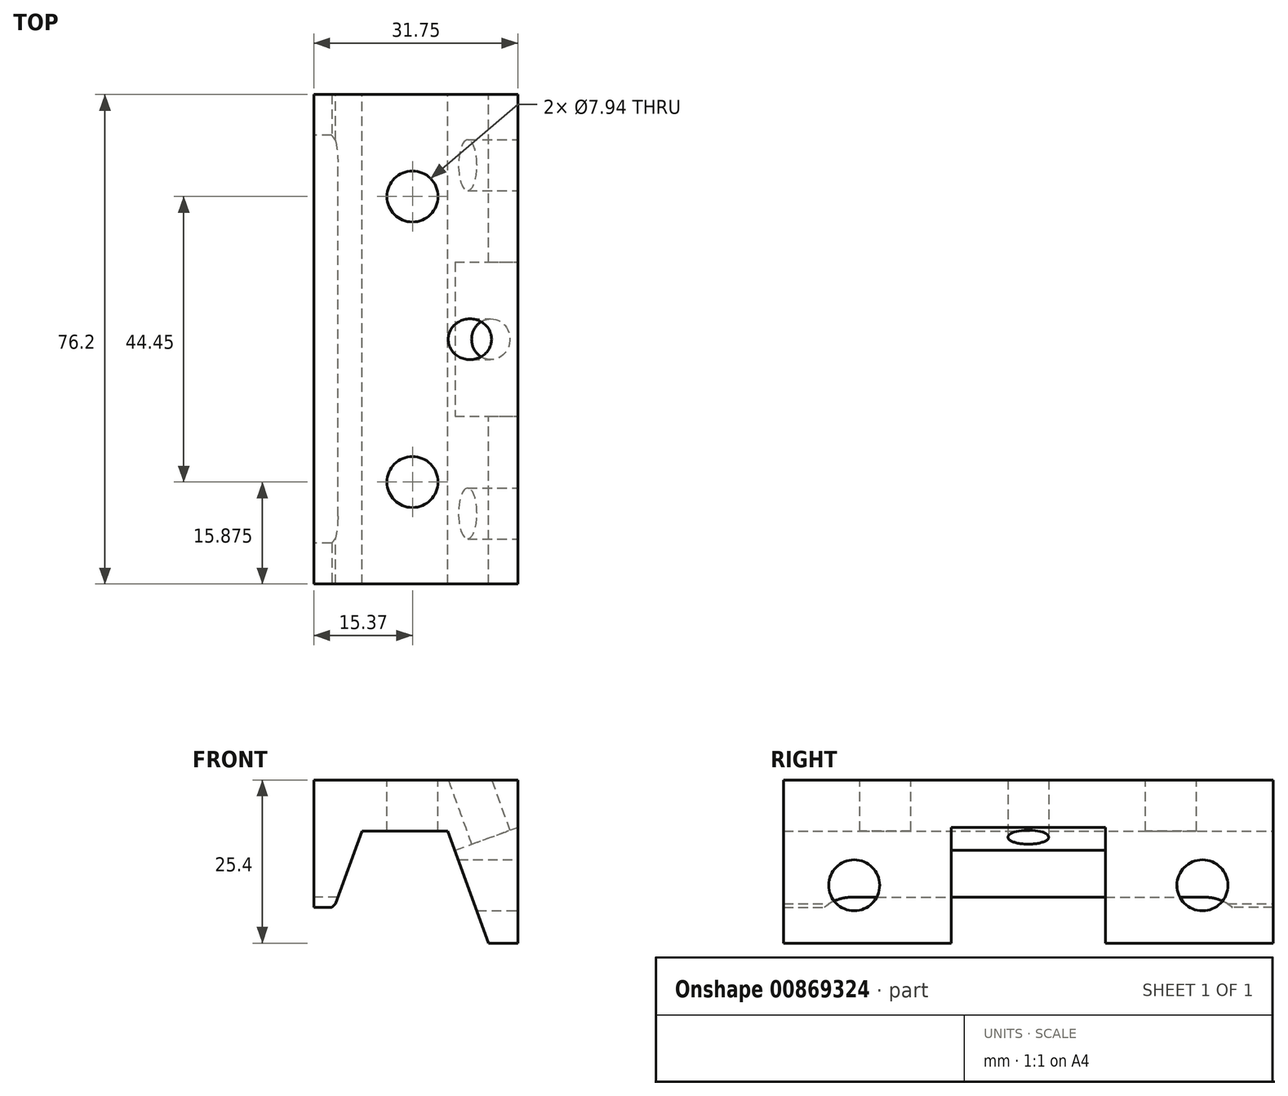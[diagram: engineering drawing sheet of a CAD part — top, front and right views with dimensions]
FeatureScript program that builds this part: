
annotation { "Feature Type Name" : "Feature", "Feature Type Description" : "" }
export const myFeature = defineFeature(function(context is Context, id is Id, definition is map)
    precondition{}
    {
        {
            var Q0;
            Q0=qCreatedBy(makeId("Front.planeOp"),FACE);
            var sketch = newSketch(context, id + "F0", { "sketchPlane" : qUnion([Q0])});
            skLineSegment(sketch, "E0", {"start": v(-7.86, 17.46) * mm, "end": v(5.5, 17.46) * mm});
            skLineSegment(sketch, "E1", {"start": v(-12.2, 5.56) * mm, "end": v(-15.37, 5.56) * mm});
            skLineSegment(sketch, "E2", {"start": v(11.86, 0) * mm, "end": v(16.38, 0) * mm});
            skLineSegment(sketch, "E3", {"start": v(-7.86, 17.46) * mm, "end": v(-12.2, 5.56) * mm});
            skLineSegment(sketch, "E4", {"start": v(5.5, 17.46) * mm, "end": v(11.86, 0) * mm});
            skPoint(sketch, "E5", {"position": v(8.69, 8.73) * mm});
            skPoint(sketch, "E5.positionSnap0", {"position": v(8.69, 8.73) * mm});
            skPoint(sketch, "E6", {"position": v(0, 17.46) * mm});
            skLineSegment(sketch, "E7", {"start": v(-15.37, 5.56) * mm, "end": v(-15.37, 25.4) * mm});
            skLineSegment(sketch, "E8", {"start": v(-15.37, 25.4) * mm, "end": v(16.38, 25.4) * mm});
            skLineSegment(sketch, "E9", {"start": v(6.6, 14.46) * mm, "end": v(16.38, 18.02) * mm});
            skLineSegment(sketch, "E10", {"start": v(29.07, 14.12) * mm, "end": v(9.34, 6.94) * mm});
            skLineSegment(sketch, "E11", {"start": v(16.38, 25.4) * mm, "end": v(16.38, 0) * mm});
            skPoint(sketch, "E12", {"position": v(19.2, 10.53) * mm});
            skSolve(sketch);
        }
        {
            var Q0;
            {var subQ0=sQuery(id+"F0.wireOp",EDGE,"wyo1lMDk-e6bC-kYg6-a8j1-Ru8ALgOuLrMR");var subQ1=sQuery(id+"F0.wireOp",EDGE,"E9");var subQ2=makeQuery(id+"F0.imprint","INTERSECT",VERTEX,{"derivedFrom":[subQ1,subQ0]});Q0=makeQuery(id+"F0.imprint","IMPRINT",FACE,{"disambiguationData":[TD([[makeQuery(id+"F0.imprint","IMPRINT",EDGE,{"disambiguationData":[TD([[subQ2,1.0]])],"derivedFrom":subQ1}),-1.0]])]});}
            var Q1;
            {var subQ5=sQuery(id+"F0.wireOp",EDGE,"E0");Q1=makeQuery(id+"F0.imprint","IMPRINT",FACE,{"disambiguationData":[TD([[makeQuery(id+"F0.imprint","IMPRINT",EDGE,{"derivedFrom":subQ5}),1.0]])]});}
            var Q2;
            {var subQ0=sQuery(id+"F0.wireOp",EDGE,"E9");var subQ1=sQuery(id+"F0.wireOp",EDGE,"E4");var subQ2=makeQuery(id+"F0.imprint","INTERSECT",VERTEX,{"derivedFrom":[subQ1,subQ0]});Q2=makeQuery(id+"F0.imprint","IMPRINT",FACE,{"disambiguationData":[TD([[makeQuery(id+"F0.imprint","IMPRINT",EDGE,{"disambiguationData":[TD([[subQ2,-1.0]])],"derivedFrom":subQ1}),1.0]])]});}
            var Q3;
            {var subQ5=sQuery(id+"F0.wireOp",EDGE,"MGBtKP5I-cxsz-jBet-ha0O-NG6443iWrkXD.bottom");Q3=makeQuery(id+"F0.imprint","IMPRINT",FACE,{"disambiguationData":[TD([[makeQuery(id+"F0.imprint","IMPRINT",EDGE,{"derivedFrom":subQ5}),1.0]])]});}
            var Q4;
            {var subQ3=sQuery(id+"F0.wireOp",EDGE,"MGBtKP5I-cxsz-jBet-ha0O-NG6443iWrkXD.left");var subQ5=sQuery(id+"F0.wireOp",EDGE,"E9");var subQ6=makeQuery(id+"F0.imprint","INTERSECT",VERTEX,{"derivedFrom":[subQ5,subQ3]});Q4=makeQuery(id+"F0.imprint","IMPRINT",FACE,{"disambiguationData":[TD([[makeQuery(id+"F0.imprint","IMPRINT",EDGE,{"disambiguationData":[TD([[subQ6,-1.0]])],"derivedFrom":subQ5}),-1.0]])]});}
            var Q5;
            {var subQ0=sQuery(id+"F0.wireOp",EDGE,"MGBtKP5I-cxsz-jBet-ha0O-NG6443iWrkXD.left");var subQ1=sQuery(id+"F0.wireOp",EDGE,"E9");var subQ2=makeQuery(id+"F0.imprint","INTERSECT",VERTEX,{"derivedFrom":[subQ1,subQ0]});Q5=makeQuery(id+"F0.imprint","IMPRINT",FACE,{"disambiguationData":[TD([[makeQuery(id+"F0.imprint","IMPRINT",EDGE,{"disambiguationData":[TD([[subQ2,-1.0]])],"derivedFrom":subQ1}),1.0]])]});}
            var Q6;
            {var subQ0=sQuery(id+"F0.wireOp",EDGE,"E11");var subQ1=sQuery(id+"F0.wireOp",EDGE,"wyo1lMDk-e6bC-kYg6-a8j1-Ru8ALgOuLrMR");var subQ2=makeQuery(id+"F0.imprint","INTERSECT",VERTEX,{"derivedFrom":[subQ1,subQ0]});Q6=makeQuery(id+"F0.imprint","IMPRINT",FACE,{"disambiguationData":[TD([[makeQuery(id+"F0.imprint","IMPRINT",EDGE,{"disambiguationData":[TD([[subQ2,1.0]])],"derivedFrom":subQ1}),1.0]])]});}
            var Q7;
            {var subQ0=sQuery(id+"F0.wireOp",EDGE,"E2");Q7=makeQuery(id+"F0.imprint","IMPRINT",FACE,{"disambiguationData":[TD([[makeQuery(id+"F0.imprint","IMPRINT",EDGE,{"derivedFrom":subQ0}),1.0]])]});}
            extrude(context, id + "F1", {"entities" : qUnion([Q0, Q1, Q2, Q3, Q4, Q5, Q6, Q7]), "endBound" : BoundingType.SYMMETRIC, "depth" : 76.2 * mm, "offsetDistance" : 25.4 * mm});
        }
        {
            var Q0;
            {var subQ0=sQuery(id+"F0.wireOp",EDGE,"E2");Q0=makeQuery(id+"F0.imprint","IMPRINT",FACE,{"disambiguationData":[TD([[makeQuery(id+"F0.imprint","IMPRINT",EDGE,{"derivedFrom":subQ0}),1.0]])]});}
            var Q1;
            {var subQ0=sQuery(id+"F0.wireOp",EDGE,"E9");Q1=makeQuery(id+"F0.imprint","IMPRINT",FACE,{"disambiguationData":[TD([[makeQuery(id+"F0.imprint","IMPRINT",EDGE,{"derivedFrom":subQ0}),-1.0]])]});}
            extrude(context, id + "F2", {"entities" : qUnion([Q0, Q1]), "operationType" : NewBodyOperationType.REMOVE, "endBound" : BoundingType.SYMMETRIC, "oppositeDirection" : true, "depth" : 24 * mm, "offsetDistance" : 25.4 * mm});
        }
        {
            var Q0;
            Q0=makeQuery(id+"F1.opExtrude","SWEPT_EDGE",EDGE,{"disambiguationData":[OSD([sQuery(id+"F0.wireOp",EDGE,"E1"),sQuery(id+"F0.wireOp",EDGE,"E3")])]});
            chamfer(context, id + "F3", {"entities" : qUnion([Q0]), "chamferType" : ChamferType.OFFSET_ANGLE, "width" : 0.64 * mm, "oppositeDirection" : false, "angle" : 25 * degree, "tangentPropagation" : true});
        }
        {
            var Q0;
            Q0=makeQuery(id+"F1.opExtrude","SWEPT_FACE",FACE,{"disambiguationData":[OSD([sQuery(id+"F0.wireOp",EDGE,"E11")])]});
            var sketch = newSketch(context, id + "F4", { "sketchPlane" : qUnion([Q0])});
            skPoint(sketch, "E13", {"position": v(-27.1, 9) * mm});
            skCircle(sketch, "E14", {"center": v(-27.1, 9) * mm, "radius": 3.97 * mm});
            skPoint(sketch, "E15", {"position": v(27.1, 9) * mm});
            skCircle(sketch, "E16", {"center": v(27.1, 9) * mm, "radius": 3.97 * mm});
            skSolve(sketch);
        }
        {
            var Q0;
            Q0=makeQuery(id+"F4.imprint","IMPRINT",FACE,{"disambiguationData":[TD([[makeQuery(id+"F4.imprint","IMPRINT",EDGE,{"derivedFrom":sQuery(id+"F4.wireOp",EDGE,"E14")}),1.0]])]});
            var Q1;
            Q1=makeQuery(id+"F4.imprint","IMPRINT",FACE,{"disambiguationData":[TD([[makeQuery(id+"F4.imprint","IMPRINT",EDGE,{"derivedFrom":sQuery(id+"F4.wireOp",EDGE,"E16")}),1.0]])]});
            extrude(context, id + "F5", {"entities" : qUnion([Q0, Q1]), "operationType" : NewBodyOperationType.REMOVE, "oppositeDirection" : true, "depth" : 22.22 * mm, "offsetDistance" : 25.4 * mm});
        }
        {
            var Q0;
            {var subQ0=sQuery(id+"F0.wireOp",EDGE,"E4");var subQ3=sQuery(id+"F0.wireOp",EDGE,"E9");Q0=makeQuery(id+"FioreutmApQ6MFU_1.boolean.opBoolean","SPLIT",FACE,{"disambiguationData":[TD([makeQuery(id+"F1.opExtrude","SWEPT_FACE",FACE,{"disambiguationData":[OSD([subQ0])]})])],"derivedFrom":makeQuery(id+"F2.boolean.opBoolean","COPY",FACE,{"derivedFrom":makeQuery(id+"F2.opExtrude","SWEPT_FACE",FACE,{"disambiguationData":[OSD([subQ3])]})})});}
            var sketch = newSketch(context, id + "F6", { "sketchPlane" : qUnion([Q0])});
            skCircle(sketch, "E17", {"center": v(17.09, 0) * mm, "radius": 3.18 * mm});
            skSolve(sketch);
        }
        {
            var Q0;
            Q0=makeQuery(id+"F6.imprint","IMPRINT",FACE,{"disambiguationData":[TD([[makeQuery(id+"F6.imprint","IMPRINT",EDGE,{"derivedFrom":sQuery(id+"F6.wireOp",EDGE,"E17")}),1.0]])]});
            extrude(context, id + "F7", {"entities" : qUnion([Q0]), "operationType" : NewBodyOperationType.REMOVE, "oppositeDirection" : true, "depth" : 25.4 * mm, "offsetDistance" : 25.4 * mm});
        }
        {
            var Q0;
            Q0=makeQuery(id+"F1.opExtrude","SWEPT_FACE",FACE,{"disambiguationData":[OSD([sQuery(id+"F0.wireOp",EDGE,"E7")])]});
            var sketch = newSketch(context, id + "F8", { "sketchPlane" : qUnion([Q0])});
            skArc(sketch, "E18", {"start": v(38.1, 5.56) * mm, "mid": v(0, 6.64) * mm, "end": v(-38.1, 5.56) * mm});
            skLineSegment(sketch, "E19", {"start": v(-27.55, 7.14) * mm, "end": v(27.55, 7.14) * mm});
            skArc(sketch, "E20", {"start": v(-27.55, 7.14) * mm, "mid": v(-29.8, 6.73) * mm, "end": v(-31.75, 5.56) * mm});
            skArc(sketch, "E21", {"start": v(27.55, 7.14) * mm, "mid": v(29.8, 6.73) * mm, "end": v(31.75, 5.56) * mm});
            skSolve(sketch);
        }
        {
            var Q0;
            {var subQ5=sQuery(id+"F8.wireOp",EDGE,"E19");Q0=makeQuery(id+"F8.imprint","IMPRINT",FACE,{"disambiguationData":[TD([[makeQuery(id+"F8.imprint","IMPRINT",EDGE,{"derivedFrom":subQ5}),-1.0]])]});}
            var Q1;
            {var subQ0=sQuery(id+"F8.wireOp",EDGE,"E21");var subQ1=sQuery(id+"F8.wireOp",EDGE,"E18");var subQ2=makeQuery(id+"F8.imprint","INTERSECT",VERTEX,{"derivedFrom":[subQ1,subQ0]});Q1=makeQuery(id+"F8.imprint","IMPRINT",FACE,{"disambiguationData":[TD([[makeQuery(id+"F8.imprint","IMPRINT",EDGE,{"disambiguationData":[TD([[subQ2,-1.0]])],"derivedFrom":subQ1}),1.0]])]});}
            extrude(context, id + "F9", {"entities" : qUnion([Q0, Q1]), "operationType" : NewBodyOperationType.REMOVE, "oppositeDirection" : true, "depth" : 6.35 * mm, "offsetDistance" : 25.4 * mm});
        }
        {
            var Q0;
            Q0=makeQuery(id+"F1.opExtrude","SWEPT_FACE",FACE,{"disambiguationData":[OSD([sQuery(id+"F0.wireOp",EDGE,"E8")])]});
            var sketch = newSketch(context, id + "F10", { "sketchPlane" : qUnion([Q0])});
            skCircle(sketch, "E22", {"center": v(0, 22.23) * mm, "radius": 3.97 * mm});
            skCircle(sketch, "E23", {"center": v(0, -22.23) * mm, "radius": 3.97 * mm});
            skSolve(sketch);
        }
        {
            var Q0;
            Q0 = qSketchRegion(id + "F10", true);
            extrude(context, id + "F11", {"entities" : qUnion([Q0]), "operationType" : NewBodyOperationType.REMOVE, "oppositeDirection" : true, "depth" : 25.4 * mm, "offsetDistance" : 25.4 * mm});
        }
    });
